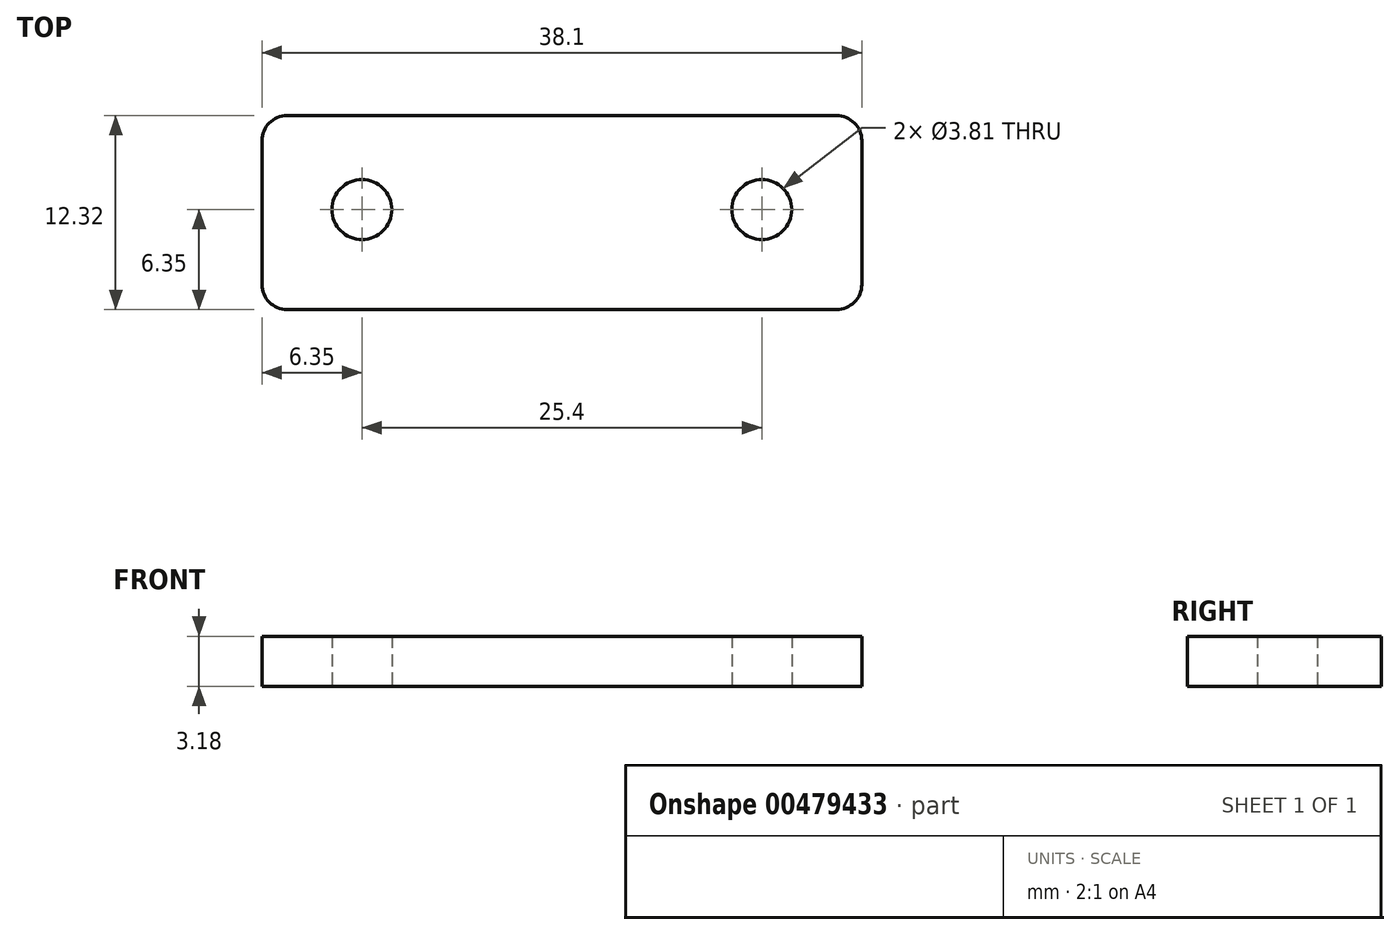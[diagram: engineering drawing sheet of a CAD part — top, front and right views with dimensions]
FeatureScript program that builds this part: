
annotation { "Feature Type Name" : "Feature", "Feature Type Description" : "" }
export const myFeature = defineFeature(function(context is Context, id is Id, definition is map)
    precondition{}
    {
        {
            var Q0;
            Q0=qCreatedBy(makeId("Top.planeOp"),FACE);
            var sketch = newSketch(context, id + "F0", { "sketchPlane" : qUnion([Q0])});
            skLineSegment(sketch, "E0.bottom", {"start": v(1.6, 0) * mm, "end": v(36.5, 0) * mm});
            skLineSegment(sketch, "E0.top", {"start": v(1.6, 12.32) * mm, "end": v(36.5, 12.32) * mm});
            skLineSegment(sketch, "E0.left", {"start": v(0, 1.6) * mm, "end": v(0, 10.72) * mm});
            skLineSegment(sketch, "E0.right", {"start": v(38.1, 1.6) * mm, "end": v(38.1, 10.72) * mm});
            skCircle(sketch, "E1", {"center": v(6.35, 6.35) * mm, "radius": 1.9 * mm});
            skCircle(sketch, "E2", {"center": v(31.75, 6.35) * mm, "radius": 1.9 * mm});
            skPoint(sketch, "E3.visualSharp", {"position": v(0, 12.32) * mm});
            skArc(sketch, "E3.filletArc", {"start": v(1.6, 12.32) * mm, "mid": v(0.47, 11.85) * mm, "end": v(0, 10.72) * mm});
            skPoint(sketch, "E4.visualSharp", {"position": v(38.1, 12.32) * mm});
            skArc(sketch, "E4.filletArc", {"start": v(38.1, 10.72) * mm, "mid": v(37.63, 11.85) * mm, "end": v(36.5, 12.32) * mm});
            skPoint(sketch, "E5.visualSharp", {"position": v(38.1, 0) * mm});
            skArc(sketch, "E5.filletArc", {"start": v(36.5, 0) * mm, "mid": v(37.63, 0.47) * mm, "end": v(38.1, 1.6) * mm});
            skPoint(sketch, "E6.visualSharp", {"position": v(0, 0) * mm});
            skArc(sketch, "E6.filletArc", {"start": v(0, 1.6) * mm, "mid": v(0.47, 0.47) * mm, "end": v(1.6, 0) * mm});
            skSolve(sketch);
        }
        {
            var Q0;
            Q0=makeQuery(id+"F0.imprint","IMPRINT",FACE,{"disambiguationData":[TD([[makeQuery(id+"F0.imprint","IMPRINT",EDGE,{"derivedFrom":sQuery(id+"F0.wireOp",EDGE,"E0.bottom")}),1.0]])]});
            extrude(context, id + "F1", {"entities" : qUnion([Q0]), "depth" : 3.17 * mm});
        }
    });
